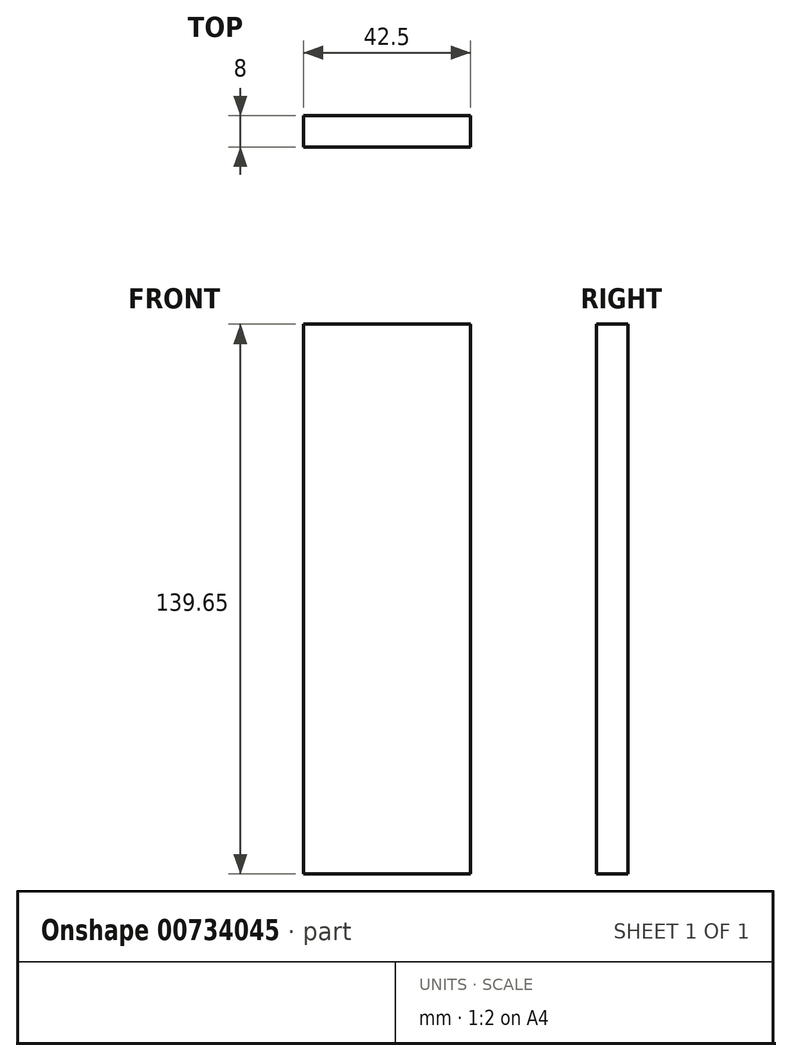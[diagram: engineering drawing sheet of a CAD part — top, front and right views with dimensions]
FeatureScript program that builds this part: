
annotation { "Feature Type Name" : "Feature", "Feature Type Description" : "" }
export const myFeature = defineFeature(function(context is Context, id is Id, definition is map)
    precondition{}
    {
        {
            var Q0;
            Q0=qCreatedBy(makeId("Front.planeOp"),FACE);
            var sketch = newSketch(context, id + "F0", { "sketchPlane" : qUnion([Q0])});
            skLineSegment(sketch, "E0.bottom", {"start": v(-19.62, 95.28) * mm, "end": v(22.88, 95.28) * mm});
            skLineSegment(sketch, "E0.top", {"start": v(-19.62, -44.37) * mm, "end": v(22.88, -44.37) * mm});
            skLineSegment(sketch, "E0.left", {"start": v(-19.62, 95.28) * mm, "end": v(-19.62, -44.37) * mm});
            skLineSegment(sketch, "E0.right", {"start": v(22.88, 95.28) * mm, "end": v(22.88, -44.37) * mm});
            skSolve(sketch);
        }
        {
            var Q0;
            Q0=qSketchRegion(id+"F0",true);
            extrude(context, id + "F1", {"entities" : qUnion([Q0]), "depth" : 8 * mm, "offsetDistance" : 25 * mm});
        }
    });
